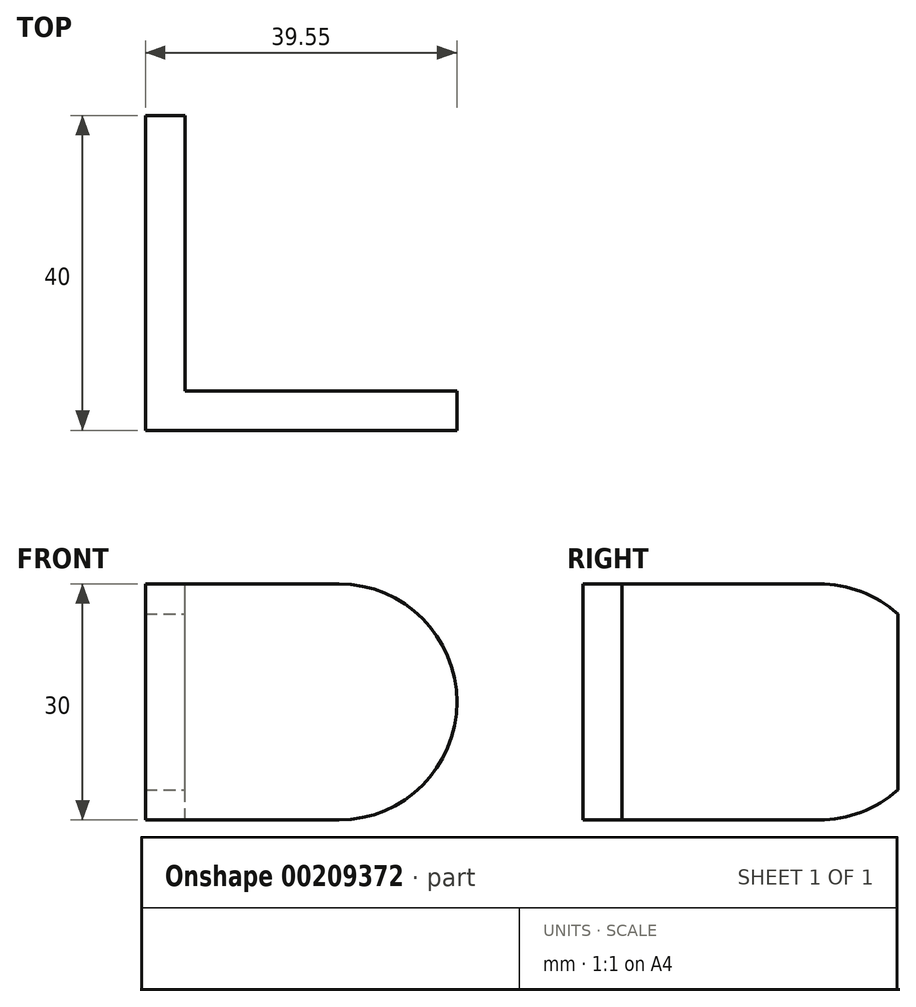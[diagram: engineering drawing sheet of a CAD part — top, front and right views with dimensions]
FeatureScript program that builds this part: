
annotation { "Feature Type Name" : "Feature", "Feature Type Description" : "" }
export const myFeature = defineFeature(function(context is Context, id is Id, definition is map)
    precondition{}
    {
        {
            var Q0;
            Q0=qCreatedBy(makeId("Top.planeOp"),FACE);
            var sketch = newSketch(context, id + "F0", { "sketchPlane" : qUnion([Q0])});
            skLineSegment(sketch, "E0.bottom", {"start": v(0, 40) * mm, "end": v(5, 40) * mm});
            skLineSegment(sketch, "E0.top", {"start": v(0, 0) * mm, "end": v(40, 0) * mm});
            skLineSegment(sketch, "E0.left", {"start": v(0, 40) * mm, "end": v(0, 0) * mm});
            skLineSegment(sketch, "E0.right", {"start": v(40, 5) * mm, "end": v(40, 0) * mm});
            skLineSegment(sketch, "E1.0", {"start": v(5, 5) * mm, "end": v(40, 5) * mm});
            skLineSegment(sketch, "E1.1", {"start": v(5, 40) * mm, "end": v(5, 5) * mm});
            skSolve(sketch);
        }
        {
            var Q0;
            Q0=makeQuery(id+"F0.imprint","IMPRINT",FACE,{"disambiguationData":[TD([[makeQuery(id+"F0.imprint","IMPRINT",EDGE,{"derivedFrom":sQuery(id+"F0.wireOp",EDGE,"E0.bottom")}),-1.0]])]});
            extrude(context, id + "F1", {"entities" : qUnion([Q0]), "oppositeDirection" : true, "depth" : 30 * mm});
        }
        {
            var Q0;
            Q0=makeQuery(id+"F1.opExtrude","SWEPT_FACE",FACE,{"disambiguationData":[OSD([sQuery(id+"F0.wireOp",EDGE,"E1.1")])]});
            var sketch = newSketch(context, id + "F2", { "sketchPlane" : qUnion([Q0])});
            skLineSegment(sketch, "E2.bottom", {"start": v(40, 0) * mm, "end": v(5, 0) * mm});
            skLineSegment(sketch, "E2.top", {"start": v(40, -30) * mm, "end": v(5, -30) * mm});
            skLineSegment(sketch, "E2.left", {"start": v(40, 0) * mm, "end": v(40, -30) * mm});
            skLineSegment(sketch, "E2.right", {"start": v(5, 0) * mm, "end": v(5, -30) * mm});
            skArc(sketch, "E3", {"start": v(30, -30) * mm, "mid": v(45, -15) * mm, "end": v(30, 0) * mm});
            skSolve(sketch);
        }
        {
            var Q0;
            {var subQ0=sQuery(id+"F2.wireOp",EDGE,"E2.left");Q0=makeQuery(id+"F2.imprint","IMPRINT",FACE,{"disambiguationData":[TD([[makeQuery(id+"F2.imprint","IMPRINT",EDGE,{"derivedFrom":subQ0}),1.0]])]});}
            extrude(context, id + "F3", {"entities" : qUnion([Q0]), "operationType" : NewBodyOperationType.REMOVE, "oppositeDirection" : true, "depth" : 15.3 * mm});
        }
        {
            var Q0;
            Q0=makeQuery(id+"F1.opExtrude","SWEPT_FACE",FACE,{"disambiguationData":[OSD([sQuery(id+"F0.wireOp",EDGE,"E1.0")])]});
            var sketch = newSketch(context, id + "F4", { "sketchPlane" : qUnion([Q0])});
            skLineSegment(sketch, "E4.bottom", {"start": v(-40, 0) * mm, "end": v(-5, 0) * mm});
            skLineSegment(sketch, "E4.top", {"start": v(-40, -30) * mm, "end": v(-5, -30) * mm});
            skLineSegment(sketch, "E4.left", {"start": v(-40, 0) * mm, "end": v(-40, -30) * mm});
            skLineSegment(sketch, "E4.right", {"start": v(-5, 0) * mm, "end": v(-5, -30) * mm});
            skArc(sketch, "E5", {"start": v(-24.55, 0) * mm, "mid": v(-39.55, -15) * mm, "end": v(-24.55, -30) * mm});
            skSolve(sketch);
        }
        {
            var Q0;
            {var subQ0=sQuery(id+"F4.wireOp",EDGE,"E4.left");Q0=makeQuery(id+"F4.imprint","IMPRINT",FACE,{"disambiguationData":[TD([[makeQuery(id+"F4.imprint","IMPRINT",EDGE,{"derivedFrom":subQ0}),-1.0]])]});}
            extrude(context, id + "F5", {"entities" : qUnion([Q0]), "operationType" : NewBodyOperationType.REMOVE, "oppositeDirection" : true, "depth" : 25 * mm});
        }
    });
